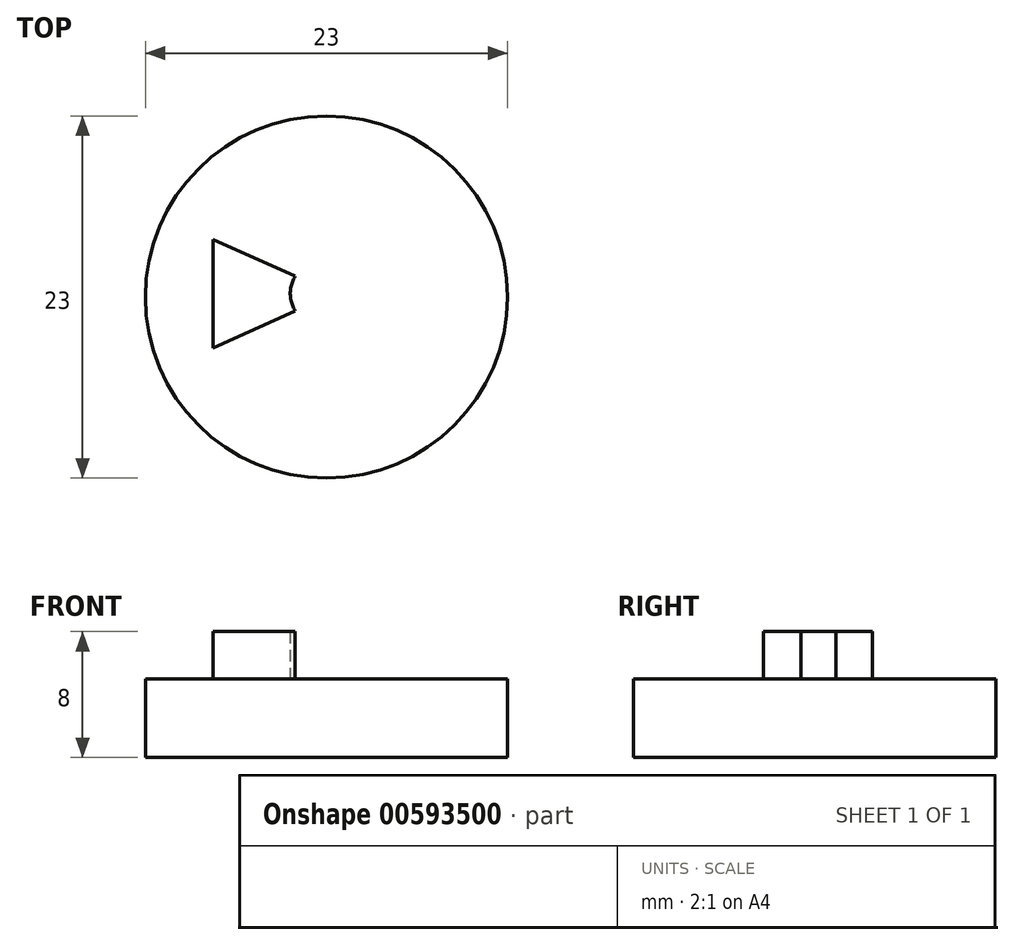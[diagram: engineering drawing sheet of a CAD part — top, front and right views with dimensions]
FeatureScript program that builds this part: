
annotation { "Feature Type Name" : "Feature", "Feature Type Description" : "" }
export const myFeature = defineFeature(function(context is Context, id is Id, definition is map)
    precondition{}
    {
        {
            var Q0;
            Q0=qCreatedBy(makeId("Top.planeOp"),FACE);
            var sketch = newSketch(context, id + "F0", { "sketchPlane" : qUnion([Q0])});
            skCircle(sketch, "E0", {"center": v(-31.16, 23.66) * mm, "radius": 11.5 * mm});
            skSolve(sketch);
        }
        {
            var Q0;
            Q0=makeQuery(id+"F0.imprint","IMPRINT",FACE,{"disambiguationData":[TD([[makeQuery(id+"F0.imprint","IMPRINT",EDGE,{"derivedFrom":sQuery(id+"F0.wireOp",EDGE,"E0")}),1.0]])]});
            extrude(context, id + "F1", {"entities" : qUnion([Q0]), "depth" : 5 * mm, "offsetDistance" : 25 * mm});
        }
        {
            var Q0;
            Q0=makeQuery(id+"F1.opExtrude","CAP_FACE",FACE,{"disambiguationData":[OSD([sQuery(id+"F0.wireOp",EDGE,"E0")])],"isStart":false});
            var sketch = newSketch(context, id + "F2", { "sketchPlane" : qUnion([Q0])});
            skPoint(sketch, "E1.endSnap0", {"position": v(-35.6, 23.87) * mm});
            skFitSpline(sketch, "E2", {"points": [v(-33.47, 23.87) * mm, v(-28.77, 27.32) * mm, v(-23.29, 23.87) * mm, v(-28.6, 20.41) * mm, v(-33.47, 23.87) * mm]});
            skPoint(sketch, "E3.orphan", {"position": v(-35.6, 27.32) * mm});
            skPoint(sketch, "E4.end.orphan", {"position": v(-35.6, 20.41) * mm});
            skPoint(sketch, "E5", {"position": v(-31.16, 23.66) * mm});
            skLineSegment(sketch, "E6", {"start": v(-38.38, 27.32) * mm, "end": v(-38.38, 20.41) * mm});
            skLineSegment(sketch, "E7", {"start": v(-38.38, 20.41) * mm, "end": v(-33.15, 22.78) * mm});
            skLineSegment(sketch, "E8", {"start": v(-38.38, 27.32) * mm, "end": v(-33.15, 25) * mm});
            skSolve(sketch);
        }
        {
            var Q0;
            Q0=makeQuery(id+"F2.imprint","IMPRINT",FACE,{"disambiguationData":[TD([[makeQuery(id+"F2.imprint","IMPRINT",EDGE,{"derivedFrom":sQuery(id+"F2.wireOp",EDGE,"E6")}),1.0]])]});
            extrude(context, id + "F3", {"entities" : qUnion([Q0]), "operationType" : NewBodyOperationType.ADD, "depth" : 3 * mm, "offsetDistance" : 25 * mm});
        }
        {
            var Q0;
            Q0=makeQuery(id+"F3.opExtrude","CAP_FACE",FACE,{"disambiguationData":[OSD([sQuery(id+"F2.wireOp",EDGE,"E2"),sQuery(id+"F2.wireOp",EDGE,"E6"),sQuery(id+"F2.wireOp",EDGE,"E7"),sQuery(id+"F2.wireOp",EDGE,"E8")])],"isStart":false});
            var sketch = newSketch(context, id + "F4", { "sketchPlane" : qUnion([Q0])});
            skCircle(sketch, "E9", {"center": v(-25.45, 24.76) * mm, "radius": 0.38 * mm});
            skSolve(sketch);
        }
        {
            var Q0;
            Q0=makeQuery(id+"F4.imprint","IMPRINT",FACE,{"disambiguationData":[TD([[makeQuery(id+"F4.imprint","IMPRINT",EDGE,{"derivedFrom":sQuery(id+"F4.wireOp",EDGE,"E9")}),1.0]])]});
            extrude(context, id + "F5", {"entities" : qUnion([Q0]), "operationType" : NewBodyOperationType.REMOVE, "oppositeDirection" : true, "depth" : 2 * mm, "offsetDistance" : 25 * mm});
        }
    });
